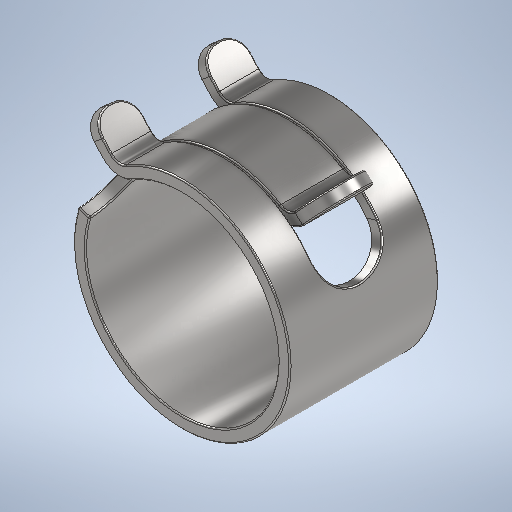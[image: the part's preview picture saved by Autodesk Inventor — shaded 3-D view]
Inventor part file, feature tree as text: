
AUTODESK INVENTOR PART (.ipt)
format: ipt  version: 2025 (Build 290162000, 162)  size: 594,432 bytes
history: native  units: mm
features: fillet x1
ambient origin geometry x8: Origin, YZ Plane, XZ Plane, XY Plane, X Axis, Y Axis, Z Axis, Center Point
bodies: Solid1 (feature_tree)
feature tree (1):
  fillet  "Fillet8"  [1 undecoded]
note: 1 required parameter value undecoded (feature->parameter linkage not recoverable at this tier; creation-order binding heuristic only, values carry confidence <= 0.55)
